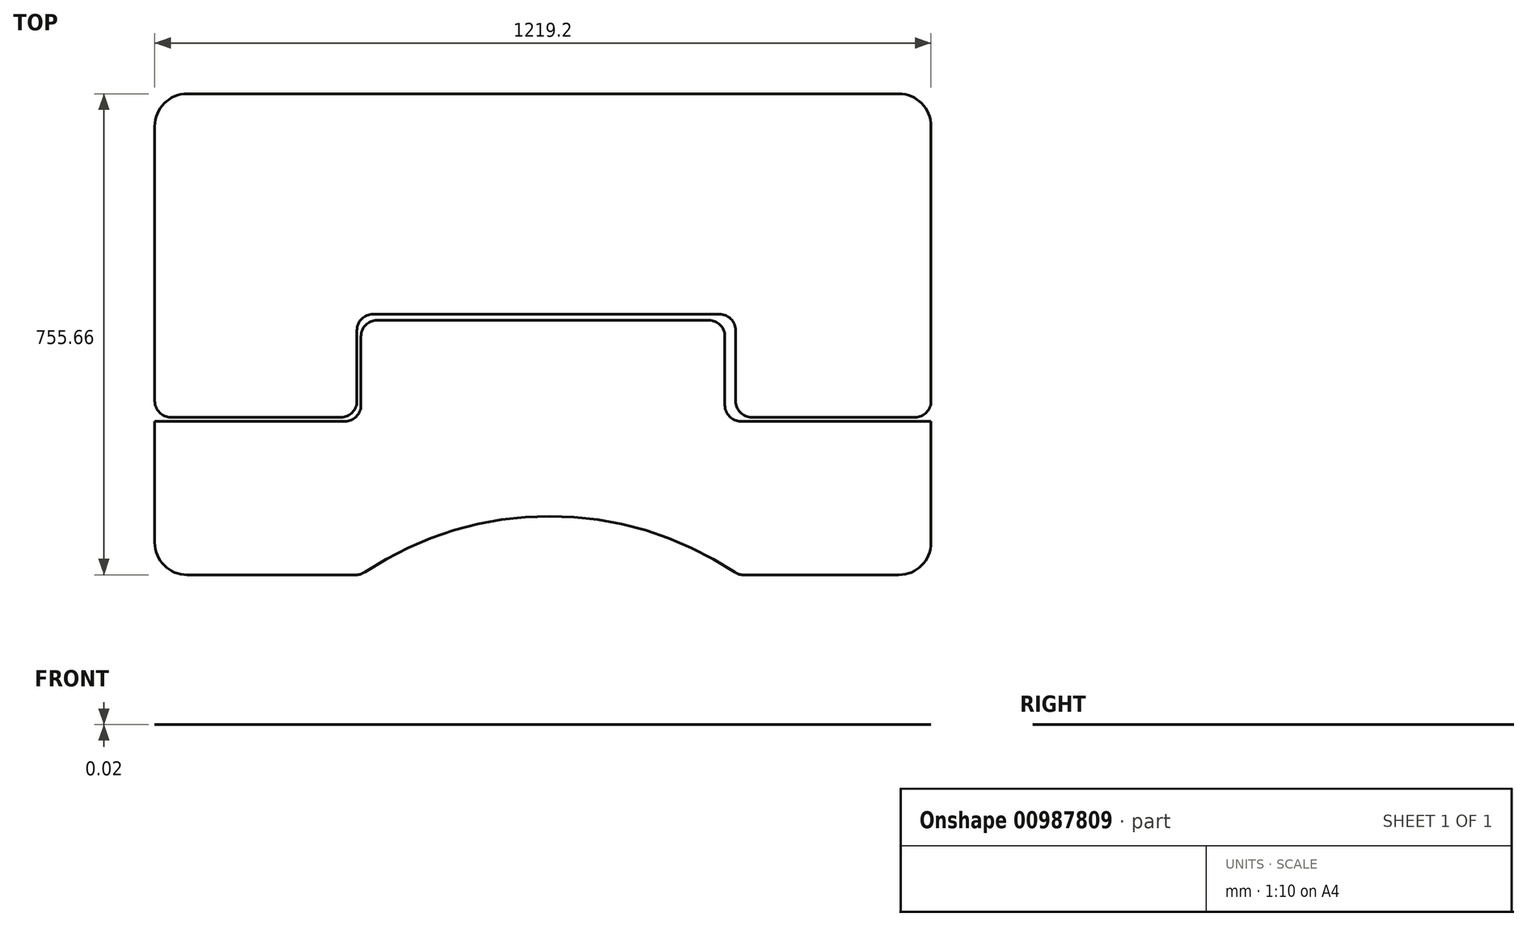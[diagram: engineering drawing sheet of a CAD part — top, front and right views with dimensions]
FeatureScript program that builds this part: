
annotation { "Feature Type Name" : "Feature", "Feature Type Description" : "" }
export const myFeature = defineFeature(function(context is Context, id is Id, definition is map)
    precondition{}
    {
        {
            var Q0;
            Q0=qCreatedBy(makeId("Top.planeOp"),FACE);
            var sketch = newSketch(context, id + "F0", { "sketchPlane" : qUnion([Q0])});
            skLineSegment(sketch, "E0.bottom", {"start": v(-294.03, -377.83) * mm, "end": v(-558.8, -377.83) * mm});
            skLineSegment(sketch, "E0.top", {"start": v(558.8, 377.83) * mm, "end": v(-558.8, 377.83) * mm});
            skLineSegment(sketch, "E0.left", {"start": v(609.6, -327.02) * mm, "end": v(609.6, -136.6) * mm});
            skLineSegment(sketch, "E0.right", {"start": v(-609.6, -327.03) * mm, "end": v(-609.6, -136.53) * mm});
            skPoint(sketch, "E0.middle", {"position": v(0, 0) * mm});
            skLineSegment(sketch, "E1", {"start": v(-609.6, -136.53) * mm, "end": v(-311.15, -136.53) * mm});
            skLineSegment(sketch, "E2", {"start": v(0, 831.15) * mm, "end": v(0, -741.97) * mm, "construction": true});
            skPoint(sketch, "E2.startSnap0", {"position": v(0, 377.83) * mm});
            skPoint(sketch, "E2.endSnap0", {"position": v(0, -377.83) * mm});
            skPoint(sketch, "E3.visualSharp", {"position": v(-609.6, 377.83) * mm});
            skArc(sketch, "E3.filletArc", {"start": v(-558.8, 377.82) * mm, "mid": v(-594.72, 362.95) * mm, "end": v(-609.6, 327.02) * mm});
            skPoint(sketch, "E4.visualSharp", {"position": v(609.6, 377.83) * mm});
            skArc(sketch, "E4.filletArc", {"start": v(609.6, 327.03) * mm, "mid": v(594.72, 362.95) * mm, "end": v(558.8, 377.83) * mm});
            skPoint(sketch, "E5.visualSharp", {"position": v(609.6, -377.82) * mm});
            skArc(sketch, "E5.filletArc", {"start": v(558.8, -377.82) * mm, "mid": v(594.72, -362.95) * mm, "end": v(609.6, -327.02) * mm});
            skPoint(sketch, "E6.visualSharp", {"position": v(-609.6, -377.83) * mm});
            skArc(sketch, "E6.filletArc", {"start": v(-609.6, -327.03) * mm, "mid": v(-594.72, -362.95) * mm, "end": v(-558.8, -377.83) * mm});
            skLineSegment(sketch, "E7", {"start": v(315.14, -377.83) * mm, "end": v(558.8, -377.83) * mm});
            skPoint(sketch, "E8.visualSharp", {"position": v(307.36, -377.83) * mm});
            skLineSegment(sketch, "E9", {"start": v(-266.7, 31.77) * mm, "end": v(277.25, 31.77) * mm});
            skLineSegment(sketch, "E10", {"start": v(302.65, 31.77) * mm, "end": v(302.65, 31.77) * mm});
            skLineSegment(sketch, "E11", {"start": v(311.15, -136.52) * mm, "end": v(609.6, -136.52) * mm});
            skPoint(sketch, "E12.third.point", {"position": v(10.55, -285.73) * mm});
            skArc(sketch, "E13.converted", {"start": v(301.06, -373.57) * mm, "mid": v(10.55, -285.73) * mm, "end": v(-279.95, -373.57) * mm});
            skLineSegment(sketch, "E14", {"start": v(302.65, 6.37) * mm, "end": v(302.65, -104.77) * mm});
            skLineSegment(sketch, "E15.0", {"start": v(328.05, -130.17) * mm, "end": v(584.2, -130.17) * mm});
            skLineSegment(sketch, "E15.2", {"start": v(-584.2, -130.18) * mm, "end": v(-317.5, -130.18) * mm});
            skLineSegment(sketch, "E16", {"start": v(-292.1, 6.37) * mm, "end": v(-292.1, -104.78) * mm});
            skLineSegment(sketch, "E17.0", {"start": v(-285.75, -3.17) * mm, "end": v(-285.75, -111.13) * mm});
            skLineSegment(sketch, "E18", {"start": v(285.75, -3.17) * mm, "end": v(285.75, -111.12) * mm});
            skLineSegment(sketch, "E19", {"start": v(-260.35, 22.23) * mm, "end": v(260.35, 22.23) * mm});
            skLineSegment(sketch, "E20", {"start": v(-609.6, -104.78) * mm, "end": v(-609.6, 327.02) * mm});
            skLineSegment(sketch, "E21", {"start": v(609.6, -104.77) * mm, "end": v(609.6, 327.03) * mm});
            skLineSegment(sketch, "E22", {"start": v(609.6, -136.6) * mm, "end": v(609.6, -136.52) * mm});
            skPoint(sketch, "E23.visualSharp", {"position": v(-609.6, -130.18) * mm});
            skArc(sketch, "E23.filletArc", {"start": v(-609.6, -104.78) * mm, "mid": v(-602.16, -122.74) * mm, "end": v(-584.2, -130.18) * mm});
            skPoint(sketch, "E24.visualSharp", {"position": v(-292.1, -130.18) * mm});
            skArc(sketch, "E24.filletArc", {"start": v(-317.5, -130.18) * mm, "mid": v(-299.54, -122.74) * mm, "end": v(-292.1, -104.78) * mm});
            skPoint(sketch, "E25.visualSharp", {"position": v(-285.75, 22.23) * mm});
            skArc(sketch, "E25.filletArc", {"start": v(-260.35, 22.23) * mm, "mid": v(-278.31, 14.79) * mm, "end": v(-285.75, -3.17) * mm});
            skPoint(sketch, "E26.visualSharp", {"position": v(-292.1, 31.77) * mm});
            skArc(sketch, "E26.filletArc", {"start": v(-266.7, 31.77) * mm, "mid": v(-284.66, 24.33) * mm, "end": v(-292.1, 6.37) * mm});
            skPoint(sketch, "E27.visualSharp", {"position": v(-285.75, -136.53) * mm});
            skArc(sketch, "E27.filletArc", {"start": v(-311.15, -136.53) * mm, "mid": v(-293.19, -129.09) * mm, "end": v(-285.75, -111.13) * mm});
            skPoint(sketch, "E28.visualSharp", {"position": v(285.75, 22.23) * mm});
            skArc(sketch, "E28.filletArc", {"start": v(285.75, -3.17) * mm, "mid": v(278.31, 14.79) * mm, "end": v(260.35, 22.23) * mm});
            skPoint(sketch, "E29.visualSharp", {"position": v(302.65, 31.77) * mm});
            skArc(sketch, "E29.filletArc", {"start": v(302.65, 6.37) * mm, "mid": v(295.22, 24.33) * mm, "end": v(277.25, 31.77) * mm});
            skPoint(sketch, "E30.visualSharp", {"position": v(302.65, -130.17) * mm});
            skArc(sketch, "E30.filletArc", {"start": v(302.65, -104.77) * mm, "mid": v(310.1, -122.74) * mm, "end": v(328.05, -130.17) * mm});
            skPoint(sketch, "E31.visualSharp", {"position": v(285.75, -136.52) * mm});
            skArc(sketch, "E31.filletArc", {"start": v(285.75, -111.12) * mm, "mid": v(293.19, -129.09) * mm, "end": v(311.15, -136.52) * mm});
            skPoint(sketch, "E32.visualSharp", {"position": v(609.6, -130.17) * mm});
            skArc(sketch, "E32.filletArc", {"start": v(584.2, -130.17) * mm, "mid": v(602.16, -122.74) * mm, "end": v(609.6, -104.77) * mm});
            skPoint(sketch, "E33.visualSharp", {"position": v(-286.25, -377.83) * mm});
            skArc(sketch, "E33.filletArc", {"start": v(-294.03, -377.83) * mm, "mid": v(-286.68, -376.74) * mm, "end": v(-279.95, -373.57) * mm});
            skArc(sketch, "E34.filletArc", {"start": v(301.06, -373.57) * mm, "mid": v(307.78, -376.74) * mm, "end": v(315.14, -377.83) * mm});
            skSolve(sketch);
        }
        {
            var Q0;
            Q0=makeQuery(id+"F0.imprint","IMPRINT",FACE,{"disambiguationData":[TD([[makeQuery(id+"F0.imprint","IMPRINT",EDGE,{"derivedFrom":sQuery(id+"F0.wireOp",EDGE,"E0.bottom")}),-1.0]])]});
            extrude(context, id + "F1", {"entities" : qUnion([Q0]), "depth" : 5 / 203.2 * mm, "offsetDistance" : 25.4 * mm});
        }
        {
            var Q0;
            Q0=makeQuery(id+"F0.imprint","IMPRINT",FACE,{"disambiguationData":[TD([[makeQuery(id+"F0.imprint","IMPRINT",EDGE,{"derivedFrom":sQuery(id+"F0.wireOp",EDGE,"E0.top")}),1.0]])]});
            extrude(context, id + "F2", {"entities" : qUnion([Q0]), "depth" : 5 / 203.2 * mm, "offsetDistance" : 25.4 * mm});
        }
    });
